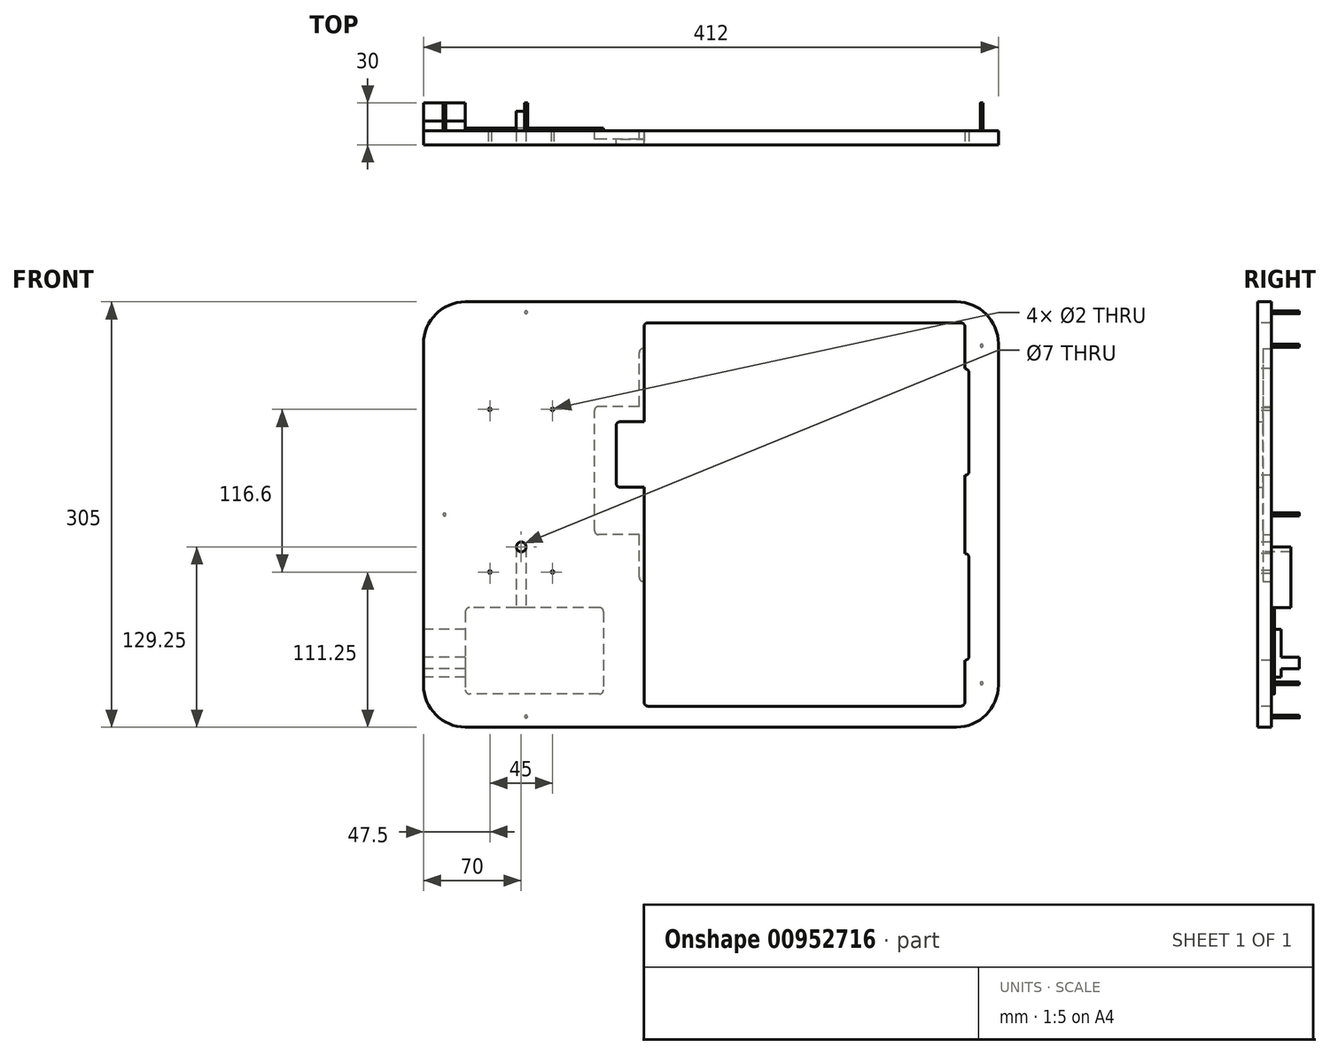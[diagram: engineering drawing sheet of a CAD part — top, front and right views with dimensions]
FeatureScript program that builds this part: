
annotation { "Feature Type Name" : "Feature", "Feature Type Description" : "" }
export const myFeature = defineFeature(function(context is Context, id is Id, definition is map)
    precondition{}
    {
        {
            var Q0;
            Q0=qCreatedBy(makeId("Front.planeOp"),FACE);
            var sketch = newSketch(context, id + "F0", { "sketchPlane" : qUnion([Q0])});
            skLineSegment(sketch, "E0.bottom", {"start": v(-206, 152.5) * mm, "end": v(206, 152.5) * mm});
            skLineSegment(sketch, "E0.top", {"start": v(-206, -152.5) * mm, "end": v(206, -152.5) * mm});
            skLineSegment(sketch, "E0.left", {"start": v(-206, 152.5) * mm, "end": v(-206, -152.5) * mm});
            skLineSegment(sketch, "E0.right", {"start": v(206, 152.5) * mm, "end": v(206, -152.5) * mm});
            skSolve(sketch);
        }
        {
            var Q0;
            Q0=makeQuery(id+"F0.imprint","IMPRINT",FACE,{"disambiguationData":[TD([[makeQuery(id+"F0.imprint","IMPRINT",EDGE,{"derivedFrom":sQuery(id+"F0.wireOp",EDGE,"E0.bottom")}),-1.0]])]});
            extrude(context, id + "F1", {"entities" : qUnion([Q0]), "depth" : 30 * mm, "offsetDistance" : 25 * mm});
        }
        {
            var Q0;
            Q0=makeQuery(id+"F1.opExtrude","CAP_FACE",FACE,{"disambiguationData":[OSD([sQuery(id+"F0.wireOp",EDGE,"E0.bottom"),sQuery(id+"F0.wireOp",EDGE,"E0.top"),sQuery(id+"F0.wireOp",EDGE,"E0.left"),sQuery(id+"F0.wireOp",EDGE,"E0.right")])],"isStart":false});
            var sketch = newSketch(context, id + "F2", { "sketchPlane" : qUnion([Q0])});
            skLineSegment(sketch, "E1.bottom", {"start": v(-48, 137.5) * mm, "end": v(182, 137.5) * mm});
            skLineSegment(sketch, "E1.top", {"start": v(-48, -137.5) * mm, "end": v(182, -137.5) * mm});
            skLineSegment(sketch, "E1.left", {"start": v(-48, 137.5) * mm, "end": v(-48, -137.5) * mm});
            skLineSegment(sketch, "E1.right", {"start": v(182, 137.5) * mm, "end": v(182, -137.5) * mm});
            skSolve(sketch);
        }
        {
            var Q0;
            Q0=qSketchRegion(id+"F2",true);
            extrude(context, id + "F3", {"entities" : qUnion([Q0]), "operationType" : NewBodyOperationType.REMOVE, "endBound" : BoundingType.UP_TO_NEXT, "oppositeDirection" : true, "depth" : 25 * mm, "offsetDistance" : 25 * mm});
        }
        {
            var Q0;
            Q0=makeQuery(id+"F3.boolean.opBoolean","COPY",EDGE,{"derivedFrom":makeQuery(id+"F3.opExtrude","SWEPT_EDGE",EDGE,{"disambiguationData":[OSD([sQuery(id+"F2.wireOp",EDGE,"E1.bottom"),sQuery(id+"F2.wireOp",EDGE,"E1.left")])]})});
            var Q1;
            Q1=makeQuery(id+"F3.boolean.opBoolean","COPY",EDGE,{"derivedFrom":makeQuery(id+"F3.opExtrude","SWEPT_EDGE",EDGE,{"disambiguationData":[OSD([sQuery(id+"F2.wireOp",EDGE,"E1.bottom"),sQuery(id+"F2.wireOp",EDGE,"E1.right")])]})});
            var Q2;
            Q2=makeQuery(id+"F3.boolean.opBoolean","COPY",EDGE,{"derivedFrom":makeQuery(id+"F3.opExtrude","SWEPT_EDGE",EDGE,{"disambiguationData":[OSD([sQuery(id+"F2.wireOp",EDGE,"E1.top"),sQuery(id+"F2.wireOp",EDGE,"E1.right")])]})});
            var Q3;
            Q3=makeQuery(id+"F3.boolean.opBoolean","COPY",EDGE,{"derivedFrom":makeQuery(id+"F3.opExtrude","SWEPT_EDGE",EDGE,{"disambiguationData":[OSD([sQuery(id+"F2.wireOp",EDGE,"E1.top"),sQuery(id+"F2.wireOp",EDGE,"E1.left")])]})});
            fillet(context, id + "F4", {"entities" : qUnion([Q0, Q1, Q2, Q3]), "radius" : 3 * mm, "tangentPropagation" : true, "allowEdgeOverflow" : false});
        }
        {
            var Q0;
            Q0=makeQuery(id+"F1.opExtrude","SWEPT_EDGE",EDGE,{"disambiguationData":[OSD([sQuery(id+"F0.wireOp",EDGE,"E0.top"),sQuery(id+"F0.wireOp",EDGE,"E0.left")])]});
            var Q1;
            Q1=makeQuery(id+"F1.opExtrude","SWEPT_EDGE",EDGE,{"disambiguationData":[OSD([sQuery(id+"F0.wireOp",EDGE,"E0.bottom"),sQuery(id+"F0.wireOp",EDGE,"E0.left")])]});
            var Q2;
            Q2=makeQuery(id+"F1.opExtrude","SWEPT_EDGE",EDGE,{"disambiguationData":[OSD([sQuery(id+"F0.wireOp",EDGE,"E0.bottom"),sQuery(id+"F0.wireOp",EDGE,"E0.right")])]});
            var Q3;
            Q3=makeQuery(id+"F1.opExtrude","SWEPT_EDGE",EDGE,{"disambiguationData":[OSD([sQuery(id+"F0.wireOp",EDGE,"E0.top"),sQuery(id+"F0.wireOp",EDGE,"E0.right")])]});
            fillet(context, id + "F5", {"entities" : qUnion([Q0, Q1, Q2, Q3]), "radius" : 30 * mm, "tangentPropagation" : true, "allowEdgeOverflow" : false});
        }
        {
            var Q0;
            Q0=makeQuery(id+"F3.boolean.opBoolean","COPY",FACE,{"derivedFrom":makeQuery(id+"F3.opExtrude","SWEPT_FACE",FACE,{"disambiguationData":[OSD([sQuery(id+"F2.wireOp",EDGE,"E1.left")])]})});
            var sketch = newSketch(context, id + "F6", { "sketchPlane" : qUnion([Q0])});
            skLineSegment(sketch, "E2.bottom", {"start": v(-26, 119) * mm, "end": v(0, 119) * mm});
            skLineSegment(sketch, "E2.top", {"start": v(-26, -48) * mm, "end": v(0, -48) * mm});
            skLineSegment(sketch, "E2.left", {"start": v(-26, 119) * mm, "end": v(-26, -48) * mm});
            skLineSegment(sketch, "E2.right", {"start": v(0, 119) * mm, "end": v(0, -48) * mm});
            skSolve(sketch);
        }
        {
            var Q0;
            Q0=makeQuery(id+"F6.imprint","IMPRINT",FACE,{"disambiguationData":[TD([[makeQuery(id+"F6.imprint","IMPRINT",EDGE,{"derivedFrom":sQuery(id+"F6.wireOp",EDGE,"E2.bottom")}),-1.0]])]});
            extrude(context, id + "F7", {"entities" : qUnion([Q0]), "operationType" : NewBodyOperationType.REMOVE, "oppositeDirection" : true, "depth" : 3.5 * mm, "offsetDistance" : 25 * mm});
        }
        {
            var Q0;
            Q0=makeQuery(id+"F7.boolean.opBoolean","COPY",EDGE,{"derivedFrom":makeQuery(id+"F7.opExtrude","CAP_EDGE",EDGE,{"disambiguationData":[OSD([sQuery(id+"F6.wireOp",EDGE,"E2.top")])],"isStart":false})});
            var Q1;
            Q1=makeQuery(id+"F7.boolean.opBoolean","COPY",EDGE,{"derivedFrom":makeQuery(id+"F7.opExtrude","CAP_EDGE",EDGE,{"disambiguationData":[OSD([sQuery(id+"F6.wireOp",EDGE,"E2.bottom")])],"isStart":false})});
            fillet(context, id + "F8", {"entities" : qUnion([Q0, Q1]), "radius" : 3 * mm, "tangentPropagation" : true, "allowEdgeOverflow" : false});
        }
        {
            var Q0;
            Q0=makeQuery(id+"F7.boolean.opBoolean","COPY",FACE,{"derivedFrom":makeQuery(id+"F7.opExtrude","CAP_FACE",FACE,{"disambiguationData":[OSD([sQuery(id+"F6.wireOp",EDGE,"E2.bottom"),sQuery(id+"F6.wireOp",EDGE,"E2.top"),sQuery(id+"F6.wireOp",EDGE,"E2.left"),sQuery(id+"F6.wireOp",EDGE,"E2.right")])],"isStart":false})});
            var sketch = newSketch(context, id + "F9", { "sketchPlane" : qUnion([Q0])});
            skLineSegment(sketch, "E3.bottom", {"start": v(-23.6, 77.5) * mm, "end": v(0, 77.5) * mm});
            skLineSegment(sketch, "E3.top", {"start": v(-23.6, -14.5) * mm, "end": v(0, -14.5) * mm});
            skLineSegment(sketch, "E3.left", {"start": v(-23.6, 77.5) * mm, "end": v(-23.6, -14.5) * mm});
            skLineSegment(sketch, "E3.right", {"start": v(0, 77.5) * mm, "end": v(0, -14.5) * mm});
            skSolve(sketch);
        }
        {
            var Q0;
            Q0=makeQuery(id+"F1.opExtrude","CAP_FACE",FACE,{"disambiguationData":[OSD([sQuery(id+"F0.wireOp",EDGE,"E0.bottom"),sQuery(id+"F0.wireOp",EDGE,"E0.top"),sQuery(id+"F0.wireOp",EDGE,"E0.left"),sQuery(id+"F0.wireOp",EDGE,"E0.right")])],"isStart":true});
            var sketch = newSketch(context, id + "F10", { "sketchPlane" : qUnion([Q0])});
            skLineSegment(sketch, "E4.bottom", {"start": v(51.5, -14.5) * mm, "end": v(83.5, -14.5) * mm});
            skLineSegment(sketch, "E4.top", {"start": v(51.5, 77.5) * mm, "end": v(83.5, 77.5) * mm});
            skLineSegment(sketch, "E4.left", {"start": v(51.5, -14.5) * mm, "end": v(51.5, 77.5) * mm});
            skLineSegment(sketch, "E4.right", {"start": v(83.5, -14.5) * mm, "end": v(83.5, 77.5) * mm});
            skSolve(sketch);
        }
        {
            var Q0;
            Q0=qSketchRegion(id+"F10",true);
            extrude(context, id + "F11", {"entities" : qUnion([Q0]), "operationType" : NewBodyOperationType.REMOVE, "oppositeDirection" : true, "depth" : 26 * mm, "offsetDistance" : 25 * mm});
        }
        {
            var Q0;
            Q0=makeQuery(id+"F11.boolean.opBoolean","COPY",EDGE,{"derivedFrom":makeQuery(id+"F11.opExtrude","SWEPT_EDGE",EDGE,{"disambiguationData":[OSD([sQuery(id+"F10.wireOp",EDGE,"E4.bottom"),sQuery(id+"F10.wireOp",EDGE,"E4.right")])]})});
            var Q1;
            Q1=makeQuery(id+"F11.boolean.opBoolean","COPY",EDGE,{"derivedFrom":makeQuery(id+"F11.opExtrude","SWEPT_EDGE",EDGE,{"disambiguationData":[OSD([sQuery(id+"F10.wireOp",EDGE,"E4.top"),sQuery(id+"F10.wireOp",EDGE,"E4.right")])]})});
            fillet(context, id + "F12", {"entities" : qUnion([Q0, Q1]), "radius" : 3 * mm, "tangentPropagation" : true, "allowEdgeOverflow" : false});
        }
        {
            var Q0;
            Q0=makeQuery(id+"F3.boolean.opBoolean","COPY",FACE,{"derivedFrom":makeQuery(id+"F3.opExtrude","SWEPT_FACE",FACE,{"disambiguationData":[OSD([sQuery(id+"F2.wireOp",EDGE,"E1.left")])]})});
            var sketch = newSketch(context, id + "F13", { "sketchPlane" : qUnion([Q0])});
            skLineSegment(sketch, "E5.bottom", {"start": v(-30, 66.5) * mm, "end": v(-26, 66.5) * mm});
            skLineSegment(sketch, "E5.top", {"start": v(-30, 19.5) * mm, "end": v(-26, 19.5) * mm});
            skLineSegment(sketch, "E5.left", {"start": v(-30, 66.5) * mm, "end": v(-30, 19.5) * mm});
            skLineSegment(sketch, "E5.right", {"start": v(-26, 66.5) * mm, "end": v(-26, 19.5) * mm});
            skSolve(sketch);
        }
        {
            var Q0;
            Q0=qSketchRegion(id+"F13",true);
            extrude(context, id + "F14", {"entities" : qUnion([Q0]), "operationType" : NewBodyOperationType.REMOVE, "oppositeDirection" : true, "depth" : 20 * mm, "offsetDistance" : 25 * mm});
        }
        {
            var Q0;
            Q0=makeQuery(id+"F14.boolean.opBoolean","COPY",EDGE,{"derivedFrom":makeQuery(id+"F14.opExtrude","CAP_EDGE",EDGE,{"disambiguationData":[OSD([sQuery(id+"F13.wireOp",EDGE,"E5.top")])],"isStart":false})});
            var Q1;
            Q1=makeQuery(id+"F14.boolean.opBoolean","COPY",EDGE,{"derivedFrom":makeQuery(id+"F14.opExtrude","CAP_EDGE",EDGE,{"disambiguationData":[OSD([sQuery(id+"F13.wireOp",EDGE,"E5.bottom")])],"isStart":false})});
            fillet(context, id + "F15", {"entities" : qUnion([Q0, Q1]), "radius" : 3 * mm, "tangentPropagation" : true, "allowEdgeOverflow" : false});
        }
        {
            var Q0;
            Q0=makeQuery(id+"F3.boolean.opBoolean","COPY",FACE,{"derivedFrom":makeQuery(id+"F3.opExtrude","SWEPT_FACE",FACE,{"disambiguationData":[OSD([sQuery(id+"F2.wireOp",EDGE,"E1.right")])]})});
            var sketch = newSketch(context, id + "F16", { "sketchPlane" : qUnion([Q0])});
            skLineSegment(sketch, "E6.bottom", {"start": v(0, -28) * mm, "end": v(30, -28) * mm});
            skLineSegment(sketch, "E6.top", {"start": v(0, -104.5) * mm, "end": v(30, -104.5) * mm});
            skLineSegment(sketch, "E6.left", {"start": v(0, -28) * mm, "end": v(0, -104.5) * mm});
            skLineSegment(sketch, "E6.right", {"start": v(30, -28) * mm, "end": v(30, -104.5) * mm});
            skLineSegment(sketch, "E7.bottom", {"start": v(0, 104.5) * mm, "end": v(30, 104.5) * mm});
            skLineSegment(sketch, "E7.top", {"start": v(0, 28) * mm, "end": v(30, 28) * mm});
            skLineSegment(sketch, "E7.left", {"start": v(0, 104.5) * mm, "end": v(0, 28) * mm});
            skLineSegment(sketch, "E7.right", {"start": v(30, 104.5) * mm, "end": v(30, 28) * mm});
            skSolve(sketch);
        }
        {
            var Q0;
            Q0=qSketchRegion(id+"F16",true);
            extrude(context, id + "F17", {"entities" : qUnion([Q0]), "operationType" : NewBodyOperationType.REMOVE, "oppositeDirection" : true, "depth" : 3 * mm, "offsetDistance" : 25 * mm});
        }
        {
            var Q0;
            Q0=makeQuery(id+"F17.boolean.opBoolean","COPY",EDGE,{"derivedFrom":makeQuery(id+"F17.opExtrude","CAP_EDGE",EDGE,{"disambiguationData":[OSD([sQuery(id+"F16.wireOp",EDGE,"E6.top")])],"isStart":false})});
            var Q1;
            Q1=makeQuery(id+"F17.boolean.opBoolean","COPY",EDGE,{"derivedFrom":makeQuery(id+"F17.opExtrude","CAP_EDGE",EDGE,{"disambiguationData":[OSD([sQuery(id+"F16.wireOp",EDGE,"E7.top")])],"isStart":false})});
            var Q2;
            Q2=makeQuery(id+"F17.boolean.opBoolean","COPY",EDGE,{"derivedFrom":makeQuery(id+"F17.opExtrude","CAP_EDGE",EDGE,{"disambiguationData":[OSD([sQuery(id+"F16.wireOp",EDGE,"E7.bottom")])],"isStart":false})});
            var Q3;
            Q3=makeQuery(id+"F17.boolean.opBoolean","COPY",EDGE,{"derivedFrom":makeQuery(id+"F17.opExtrude","CAP_EDGE",EDGE,{"disambiguationData":[OSD([sQuery(id+"F16.wireOp",EDGE,"E6.bottom")])],"isStart":false})});
            fillet(context, id + "F18", {"entities" : qUnion([Q0, Q1, Q2, Q3]), "radius" : 3 * mm, "tangentPropagation" : true, "allowEdgeOverflow" : false});
        }
        {
            var Q0;
            Q0=makeQuery(id+"F1.opExtrude","CAP_FACE",FACE,{"disambiguationData":[OSD([sQuery(id+"F0.wireOp",EDGE,"E0.bottom"),sQuery(id+"F0.wireOp",EDGE,"E0.top"),sQuery(id+"F0.wireOp",EDGE,"E0.left"),sQuery(id+"F0.wireOp",EDGE,"E0.right")])],"isStart":false});
            var sketch = newSketch(context, id + "F19", { "sketchPlane" : qUnion([Q0])});
            skCircle(sketch, "E8", {"center": v(-136, -23.25) * mm, "radius": 3.5 * mm});
            skSolve(sketch);
        }
        {
            var Q0;
            Q0=qSketchRegion(id+"F19",true);
            extrude(context, id + "F20", {"entities" : qUnion([Q0]), "operationType" : NewBodyOperationType.REMOVE, "oppositeDirection" : true, "depth" : 30 * mm, "offsetDistance" : 25 * mm});
        }
        {
            var Q0;
            Q0=makeQuery(id+"F1.opExtrude","CAP_FACE",FACE,{"disambiguationData":[OSD([sQuery(id+"F0.wireOp",EDGE,"E0.bottom"),sQuery(id+"F0.wireOp",EDGE,"E0.top"),sQuery(id+"F0.wireOp",EDGE,"E0.left"),sQuery(id+"F0.wireOp",EDGE,"E0.right")])],"isStart":true});
            var sketch = newSketch(context, id + "F21", { "sketchPlane" : qUnion([Q0])});
            skLineSegment(sketch, "E9.bottom", {"start": v(77, -66.75) * mm, "end": v(176, -66.75) * mm});
            skLineSegment(sketch, "E9.top", {"start": v(77, -128.75) * mm, "end": v(176, -128.75) * mm});
            skLineSegment(sketch, "E9.left", {"start": v(77, -66.75) * mm, "end": v(77, -128.75) * mm});
            skLineSegment(sketch, "E9.right", {"start": v(176, -66.75) * mm, "end": v(176, -128.75) * mm});
            skSolve(sketch);
        }
        {
            var Q0;
            Q0=qSketchRegion(id+"F21",true);
            var Q1;
            Q1=qSketchRegion(id+"F24",true);
            extrude(context, id + "F22", {"entities" : qUnion([Q0, Q1]), "operationType" : NewBodyOperationType.REMOVE, "oppositeDirection" : true, "depth" : 18 * mm, "offsetDistance" : 25 * mm});
        }
        {
            var Q0;
            Q0=makeQuery(id+"F22.boolean.opBoolean","COPY",EDGE,{"derivedFrom":makeQuery(id+"F22.opExtrude","SWEPT_EDGE",EDGE,{"disambiguationData":[OSD([sQuery(id+"F21.wireOp",EDGE,"E9.top"),sQuery(id+"F21.wireOp",EDGE,"E9.right")])]})});
            var Q1;
            Q1=makeQuery(id+"F22.boolean.opBoolean","COPY",EDGE,{"derivedFrom":makeQuery(id+"F22.opExtrude","SWEPT_EDGE",EDGE,{"disambiguationData":[OSD([sQuery(id+"F21.wireOp",EDGE,"E9.top"),sQuery(id+"F21.wireOp",EDGE,"E9.left")])]})});
            var Q2;
            Q2=makeQuery(id+"F22.boolean.opBoolean","COPY",EDGE,{"derivedFrom":makeQuery(id+"F22.opExtrude","SWEPT_EDGE",EDGE,{"disambiguationData":[OSD([sQuery(id+"F21.wireOp",EDGE,"E9.bottom"),sQuery(id+"F21.wireOp",EDGE,"E9.left")])]})});
            var Q3;
            Q3=makeQuery(id+"F22.boolean.opBoolean","COPY",EDGE,{"derivedFrom":makeQuery(id+"F22.opExtrude","SWEPT_EDGE",EDGE,{"disambiguationData":[OSD([sQuery(id+"F21.wireOp",EDGE,"E9.bottom"),sQuery(id+"F21.wireOp",EDGE,"E9.right")])]})});
            fillet(context, id + "F23", {"entities" : qUnion([Q0, Q1, Q2, Q3]), "radius" : 3 * mm, "tangentPropagation" : true, "allowEdgeOverflow" : false});
        }
        {
            var Q0;
            Q0=makeQuery(id+"F1.opExtrude","CAP_FACE",FACE,{"disambiguationData":[OSD([sQuery(id+"F0.wireOp",EDGE,"E0.bottom"),sQuery(id+"F0.wireOp",EDGE,"E0.top"),sQuery(id+"F0.wireOp",EDGE,"E0.left"),sQuery(id+"F0.wireOp",EDGE,"E0.right")])],"isStart":true});
            var sketch = newSketch(context, id + "F24", { "sketchPlane" : qUnion([Q0])});
            skLineSegment(sketch, "E10", {"start": v(132.5, -23.25) * mm, "end": v(132.5, -66.75) * mm});
            skLineSegment(sketch, "E11", {"start": v(139.5, -23.25) * mm, "end": v(139.5, -66.75) * mm});
            skSolve(sketch);
        }
        {
            var Q0;
            {var subQ0=sQuery(id+"F24.wireOp",EDGE,"E10");Q0=makeQuery(id+"F24.imprint","IMPRINT",FACE,{"disambiguationData":[TD([[makeQuery(id+"F24.imprint","IMPRINT",EDGE,{"derivedFrom":subQ0}),1.0]])]});}
            extrude(context, id + "F25", {"entities" : qUnion([Q0]), "operationType" : NewBodyOperationType.REMOVE, "oppositeDirection" : true, "depth" : 6 * mm, "offsetDistance" : 25 * mm});
        }
        {
            var Q0;
            Q0=makeQuery(id+"F1.opExtrude","SWEPT_FACE",FACE,{"disambiguationData":[OSD([sQuery(id+"F0.wireOp",EDGE,"E0.left")])]});
            var sketch = newSketch(context, id + "F26", { "sketchPlane" : qUnion([Q0])});
            skLineSegment(sketch, "E12.bottom", {"start": v(0, -82.5) * mm, "end": v(13, -82.5) * mm});
            skLineSegment(sketch, "E12.top", {"start": v(0, -102.5) * mm, "end": v(13, -102.5) * mm});
            skLineSegment(sketch, "E12.left", {"start": v(0, -82.5) * mm, "end": v(0, -102.5) * mm});
            skLineSegment(sketch, "E12.right", {"start": v(13, -82.5) * mm, "end": v(13, -102.5) * mm});
            skLineSegment(sketch, "E13.bottom", {"start": v(0, -110.5) * mm, "end": v(13, -110.5) * mm});
            skLineSegment(sketch, "E13.top", {"start": v(0, -116.5) * mm, "end": v(13, -116.5) * mm});
            skLineSegment(sketch, "E13.left", {"start": v(0, -110.5) * mm, "end": v(0, -116.5) * mm});
            skLineSegment(sketch, "E13.right", {"start": v(13, -110.5) * mm, "end": v(13, -116.5) * mm});
            skSolve(sketch);
        }
        {
            var Q0;
            Q0=qSketchRegion(id+"F26",true);
            extrude(context, id + "F27", {"entities" : qUnion([Q0]), "operationType" : NewBodyOperationType.REMOVE, "oppositeDirection" : true, "depth" : 30 * mm, "offsetDistance" : 25 * mm});
        }
        {
            var Q0;
            Q0=makeQuery(id+"F1.opExtrude","CAP_FACE",FACE,{"disambiguationData":[OSD([sQuery(id+"F0.wireOp",EDGE,"E0.bottom"),sQuery(id+"F0.wireOp",EDGE,"E0.top"),sQuery(id+"F0.wireOp",EDGE,"E0.left"),sQuery(id+"F0.wireOp",EDGE,"E0.right")])],"isStart":false});
            var sketch = newSketch(context, id + "F28", { "sketchPlane" : qUnion([Q0])});
            skCircle(sketch, "E14", {"center": v(-158.5, 75.35) * mm, "radius": 1 * mm});
            skCircle(sketch, "E15", {"center": v(-158.5, -41.25) * mm, "radius": 1 * mm});
            skCircle(sketch, "E16", {"center": v(-113.5, -41.25) * mm, "radius": 1 * mm});
            skCircle(sketch, "E17", {"center": v(-113.5, 75.35) * mm, "radius": 1 * mm});
            skLineSegment(sketch, "E18", {"start": v(-136, 61.68) * mm, "end": v(-136, -18.85) * mm});
            skLineSegment(sketch, "E19", {"start": v(-170.25, 91.95) * mm, "end": v(-101.06, 91.95) * mm});
            skSolve(sketch);
        }
        {
            var Q0;
            Q0=qSketchRegion(id+"F28",true);
            extrude(context, id + "F29", {"entities" : qUnion([Q0]), "operationType" : NewBodyOperationType.REMOVE, "oppositeDirection" : true, "depth" : 30 * mm, "offsetDistance" : 25 * mm});
        }
        {
            var Q0;
            {var subQ1=sQuery(id+"F0.wireOp",EDGE,"E0.right");var subQ2=sQuery(id+"F0.wireOp",EDGE,"E0.top");var subQ5=sQuery(id+"F0.wireOp",EDGE,"E0.left");var subQ8=sQuery(id+"F0.wireOp",EDGE,"E0.bottom");Q0=makeQuery(id+"F27.boolean.opBoolean","SPLIT",FACE,{"disambiguationData":[TD([makeQuery(id+"F1.opExtrude","SWEPT_FACE",FACE,{"disambiguationData":[OSD([subQ8])]})])],"derivedFrom":makeQuery(id+"F1.opExtrude","CAP_FACE",FACE,{"disambiguationData":[OSD([subQ8,subQ2,subQ5,subQ1])],"isStart":true})});}
            var sketch = newSketch(context, id + "F30", { "sketchPlane" : qUnion([Q0])});
            skLineSegment(sketch, "E20.bottom", {"start": v(191, 145) * mm, "end": v(-194, 145) * mm});
            skLineSegment(sketch, "E20.top", {"start": v(191, -145) * mm, "end": v(-194, -145) * mm});
            skLineSegment(sketch, "E20.left", {"start": v(191, 145) * mm, "end": v(191, -145) * mm});
            skLineSegment(sketch, "E20.right", {"start": v(-194, 145) * mm, "end": v(-194, -145) * mm});
            skCircle(sketch, "E21", {"center": v(-194, 121) * mm, "radius": 1 * mm});
            skCircle(sketch, "E22", {"center": v(-194, 0) * mm, "radius": 1 * mm});
            skCircle(sketch, "E23", {"center": v(-194, -121) * mm, "radius": 1 * mm});
            skCircle(sketch, "E24", {"center": v(-67, 145) * mm, "radius": 1 * mm});
            skPoint(sketch, "E24.centerSnap0", {"position": v(-67, 137.5) * mm});
            skCircle(sketch, "E25", {"center": v(-67, -145) * mm, "radius": 1 * mm});
            skCircle(sketch, "E26", {"center": v(132.5, -145) * mm, "radius": 1 * mm});
            skCircle(sketch, "E27", {"center": v(132.5, 145) * mm, "radius": 1 * mm});
            skCircle(sketch, "E28", {"center": v(191, 0) * mm, "radius": 1 * mm});
            skSolve(sketch);
        }
        {
            var Q0;
            {var subQ0=sQuery(id+"F30.wireOp",EDGE,"E21");var subQ1=sQuery(id+"F30.wireOp",EDGE,"E20.right");var subQ2=makeQuery(id+"F30.imprint","INTERSECT",VERTEX,{"disambiguationData":[OD(0.0)],"derivedFrom":[subQ1,subQ0]});Q0=makeQuery(id+"F30.imprint","IMPRINT",FACE,{"disambiguationData":[TD([[makeQuery(id+"F30.imprint","IMPRINT",EDGE,{"disambiguationData":[TD([[subQ2,-1.0]])],"derivedFrom":subQ1}),-1.0]])]});}
            var Q1;
            {var subQ0=sQuery(id+"F30.wireOp",EDGE,"E21");var subQ1=sQuery(id+"F30.wireOp",EDGE,"E20.right");var subQ2=makeQuery(id+"F30.imprint","INTERSECT",VERTEX,{"disambiguationData":[OD(0.0)],"derivedFrom":[subQ1,subQ0]});Q1=makeQuery(id+"F30.imprint","IMPRINT",FACE,{"disambiguationData":[TD([[makeQuery(id+"F30.imprint","IMPRINT",EDGE,{"disambiguationData":[TD([[subQ2,-1.0]])],"derivedFrom":subQ1}),1.0]])]});}
            var Q2;
            {var subQ0=sQuery(id+"F30.wireOp",EDGE,"E24");var subQ1=sQuery(id+"F30.wireOp",EDGE,"E20.bottom");var subQ2=makeQuery(id+"F30.imprint","INTERSECT",VERTEX,{"disambiguationData":[OD(0.0)],"derivedFrom":[subQ1,subQ0]});Q2=makeQuery(id+"F30.imprint","IMPRINT",FACE,{"disambiguationData":[TD([[makeQuery(id+"F30.imprint","IMPRINT",EDGE,{"disambiguationData":[TD([[subQ2,-1.0]])],"derivedFrom":subQ1}),1.0]])]});}
            var Q3;
            {var subQ0=sQuery(id+"F30.wireOp",EDGE,"E24");var subQ1=sQuery(id+"F30.wireOp",EDGE,"E20.bottom");var subQ2=makeQuery(id+"F30.imprint","INTERSECT",VERTEX,{"disambiguationData":[OD(0.0)],"derivedFrom":[subQ1,subQ0]});Q3=makeQuery(id+"F30.imprint","IMPRINT",FACE,{"disambiguationData":[TD([[makeQuery(id+"F30.imprint","IMPRINT",EDGE,{"disambiguationData":[TD([[subQ2,-1.0]])],"derivedFrom":subQ1}),-1.0]])]});}
            var Q4;
            {var subQ0=sQuery(id+"F30.wireOp",EDGE,"E27");var subQ1=sQuery(id+"F30.wireOp",EDGE,"E20.bottom");var subQ2=makeQuery(id+"F30.imprint","INTERSECT",VERTEX,{"disambiguationData":[OD(0.0)],"derivedFrom":[subQ1,subQ0]});Q4=makeQuery(id+"F30.imprint","IMPRINT",FACE,{"disambiguationData":[TD([[makeQuery(id+"F30.imprint","IMPRINT",EDGE,{"disambiguationData":[TD([[subQ2,-1.0]])],"derivedFrom":subQ1}),-1.0]])]});}
            var Q5;
            {var subQ0=sQuery(id+"F30.wireOp",EDGE,"E27");var subQ1=sQuery(id+"F30.wireOp",EDGE,"E20.bottom");var subQ2=makeQuery(id+"F30.imprint","INTERSECT",VERTEX,{"disambiguationData":[OD(0.0)],"derivedFrom":[subQ1,subQ0]});Q5=makeQuery(id+"F30.imprint","IMPRINT",FACE,{"disambiguationData":[TD([[makeQuery(id+"F30.imprint","IMPRINT",EDGE,{"disambiguationData":[TD([[subQ2,-1.0]])],"derivedFrom":subQ1}),1.0]])]});}
            var Q6;
            {var subQ0=sQuery(id+"F30.wireOp",EDGE,"E28");var subQ1=sQuery(id+"F30.wireOp",EDGE,"E20.left");var subQ2=makeQuery(id+"F30.imprint","INTERSECT",VERTEX,{"disambiguationData":[OD(0.0)],"derivedFrom":[subQ1,subQ0]});Q6=makeQuery(id+"F30.imprint","IMPRINT",FACE,{"disambiguationData":[TD([[makeQuery(id+"F30.imprint","IMPRINT",EDGE,{"disambiguationData":[TD([[subQ2,-1.0]])],"derivedFrom":subQ1}),1.0]])]});}
            var Q7;
            {var subQ0=sQuery(id+"F30.wireOp",EDGE,"E28");var subQ1=sQuery(id+"F30.wireOp",EDGE,"E20.left");var subQ2=makeQuery(id+"F30.imprint","INTERSECT",VERTEX,{"disambiguationData":[OD(0.0)],"derivedFrom":[subQ1,subQ0]});Q7=makeQuery(id+"F30.imprint","IMPRINT",FACE,{"disambiguationData":[TD([[makeQuery(id+"F30.imprint","IMPRINT",EDGE,{"disambiguationData":[TD([[subQ2,-1.0]])],"derivedFrom":subQ1}),-1.0]])]});}
            var Q8;
            {var subQ0=sQuery(id+"F30.wireOp",EDGE,"E26");var subQ1=sQuery(id+"F30.wireOp",EDGE,"E20.top");var subQ2=makeQuery(id+"F30.imprint","INTERSECT",VERTEX,{"disambiguationData":[OD(0.0)],"derivedFrom":[subQ1,subQ0]});Q8=makeQuery(id+"F30.imprint","IMPRINT",FACE,{"disambiguationData":[TD([[makeQuery(id+"F30.imprint","IMPRINT",EDGE,{"disambiguationData":[TD([[subQ2,-1.0]])],"derivedFrom":subQ1}),-1.0]])]});}
            var Q9;
            {var subQ0=sQuery(id+"F30.wireOp",EDGE,"E26");var subQ1=sQuery(id+"F30.wireOp",EDGE,"E20.top");var subQ2=makeQuery(id+"F30.imprint","INTERSECT",VERTEX,{"disambiguationData":[OD(0.0)],"derivedFrom":[subQ1,subQ0]});Q9=makeQuery(id+"F30.imprint","IMPRINT",FACE,{"disambiguationData":[TD([[makeQuery(id+"F30.imprint","IMPRINT",EDGE,{"disambiguationData":[TD([[subQ2,-1.0]])],"derivedFrom":subQ1}),1.0]])]});}
            var Q10;
            {var subQ0=sQuery(id+"F30.wireOp",EDGE,"E25");var subQ1=sQuery(id+"F30.wireOp",EDGE,"E20.top");var subQ2=makeQuery(id+"F30.imprint","INTERSECT",VERTEX,{"disambiguationData":[OD(0.0)],"derivedFrom":[subQ1,subQ0]});Q10=makeQuery(id+"F30.imprint","IMPRINT",FACE,{"disambiguationData":[TD([[makeQuery(id+"F30.imprint","IMPRINT",EDGE,{"disambiguationData":[TD([[subQ2,-1.0]])],"derivedFrom":subQ1}),-1.0]])]});}
            var Q11;
            {var subQ0=sQuery(id+"F30.wireOp",EDGE,"E25");var subQ1=sQuery(id+"F30.wireOp",EDGE,"E20.top");var subQ2=makeQuery(id+"F30.imprint","INTERSECT",VERTEX,{"disambiguationData":[OD(0.0)],"derivedFrom":[subQ1,subQ0]});Q11=makeQuery(id+"F30.imprint","IMPRINT",FACE,{"disambiguationData":[TD([[makeQuery(id+"F30.imprint","IMPRINT",EDGE,{"disambiguationData":[TD([[subQ2,-1.0]])],"derivedFrom":subQ1}),1.0]])]});}
            var Q12;
            {var subQ0=sQuery(id+"F30.wireOp",EDGE,"E23");var subQ1=sQuery(id+"F30.wireOp",EDGE,"E20.right");var subQ2=makeQuery(id+"F30.imprint","INTERSECT",VERTEX,{"disambiguationData":[OD(0.0)],"derivedFrom":[subQ1,subQ0]});Q12=makeQuery(id+"F30.imprint","IMPRINT",FACE,{"disambiguationData":[TD([[makeQuery(id+"F30.imprint","IMPRINT",EDGE,{"disambiguationData":[TD([[subQ2,-1.0]])],"derivedFrom":subQ1}),1.0]])]});}
            var Q13;
            {var subQ0=sQuery(id+"F30.wireOp",EDGE,"E23");var subQ1=sQuery(id+"F30.wireOp",EDGE,"E20.right");var subQ2=makeQuery(id+"F30.imprint","INTERSECT",VERTEX,{"disambiguationData":[OD(0.0)],"derivedFrom":[subQ1,subQ0]});Q13=makeQuery(id+"F30.imprint","IMPRINT",FACE,{"disambiguationData":[TD([[makeQuery(id+"F30.imprint","IMPRINT",EDGE,{"disambiguationData":[TD([[subQ2,-1.0]])],"derivedFrom":subQ1}),-1.0]])]});}
            var Q14;
            {var subQ0=sQuery(id+"F30.wireOp",EDGE,"E22");var subQ1=sQuery(id+"F30.wireOp",EDGE,"E20.right");var subQ2=makeQuery(id+"F30.imprint","INTERSECT",VERTEX,{"disambiguationData":[OD(0.0)],"derivedFrom":[subQ1,subQ0]});Q14=makeQuery(id+"F30.imprint","IMPRINT",FACE,{"disambiguationData":[TD([[makeQuery(id+"F30.imprint","IMPRINT",EDGE,{"disambiguationData":[TD([[subQ2,-1.0]])],"derivedFrom":subQ1}),-1.0]])]});}
            var Q15;
            {var subQ0=sQuery(id+"F30.wireOp",EDGE,"E22");var subQ1=sQuery(id+"F30.wireOp",EDGE,"E20.right");var subQ2=makeQuery(id+"F30.imprint","INTERSECT",VERTEX,{"disambiguationData":[OD(0.0)],"derivedFrom":[subQ1,subQ0]});Q15=makeQuery(id+"F30.imprint","IMPRINT",FACE,{"disambiguationData":[TD([[makeQuery(id+"F30.imprint","IMPRINT",EDGE,{"disambiguationData":[TD([[subQ2,-1.0]])],"derivedFrom":subQ1}),1.0]])]});}
            extrude(context, id + "F31", {"entities" : qUnion([Q0, Q1, Q2, Q3, Q4, Q5, Q6, Q7, Q8, Q9, Q10, Q11, Q12, Q13, Q14, Q15]), "operationType" : NewBodyOperationType.REMOVE, "oppositeDirection" : true, "depth" : 20 * mm, "offsetDistance" : 25 * mm});
        }
    });
